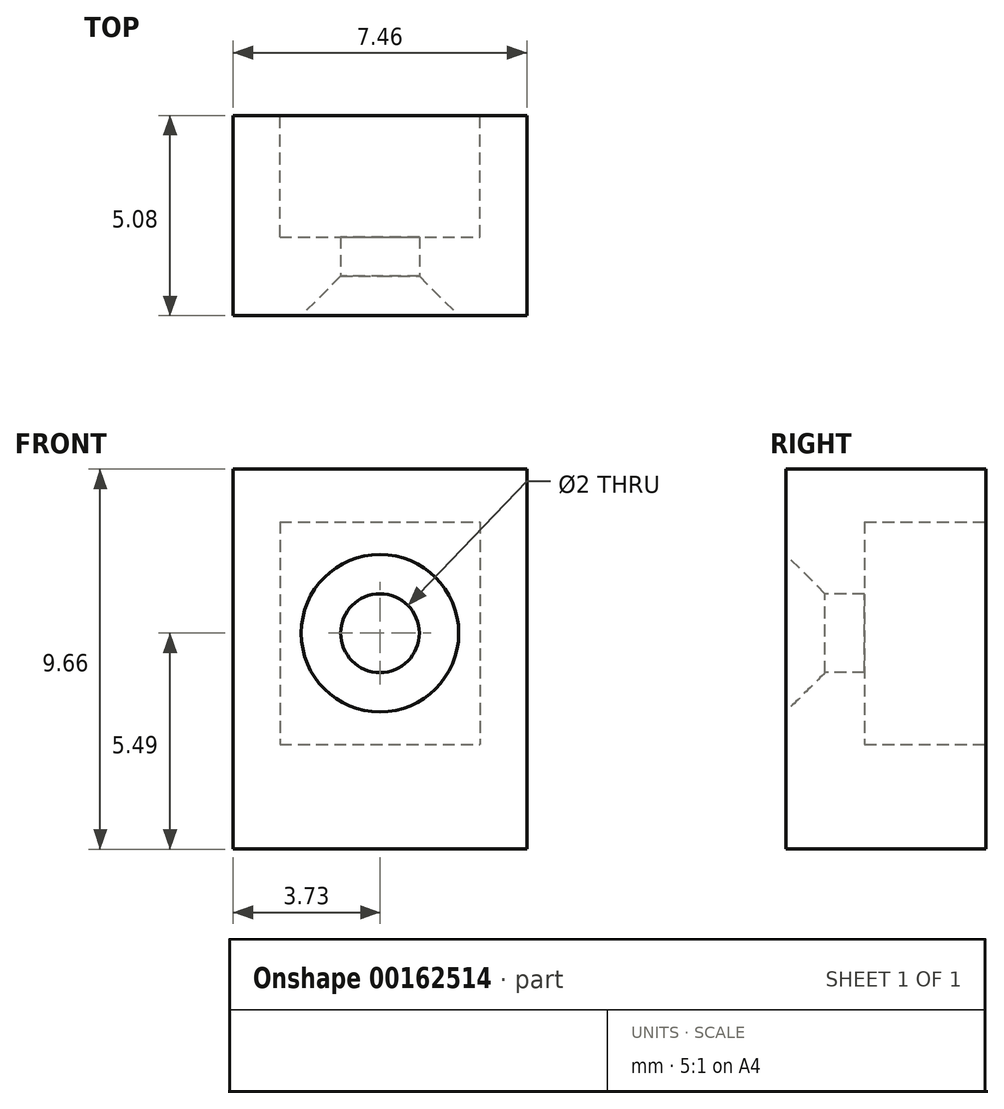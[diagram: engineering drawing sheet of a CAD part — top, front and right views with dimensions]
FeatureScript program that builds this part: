
annotation { "Feature Type Name" : "Feature", "Feature Type Description" : "" }
export const myFeature = defineFeature(function(context is Context, id is Id, definition is map)
    precondition{}
    {
        {
            var Q0;
            Q0=qCreatedBy(makeId("Front.planeOp"),FACE);
            var sketch = newSketch(context, id + "F0", { "sketchPlane" : qUnion([Q0])});
            skLineSegment(sketch, "E0.bottom", {"start": v(3.73, 4.83) * mm, "end": v(-3.73, 4.83) * mm});
            skLineSegment(sketch, "E0.top", {"start": v(3.73, -4.83) * mm, "end": v(-3.73, -4.83) * mm});
            skLineSegment(sketch, "E0.left", {"start": v(3.73, 4.83) * mm, "end": v(3.73, -4.83) * mm});
            skLineSegment(sketch, "E0.right", {"start": v(-3.73, 4.83) * mm, "end": v(-3.73, -4.83) * mm});
            skPoint(sketch, "E0.middle", {"position": v(0, 0) * mm});
            skCircle(sketch, "E1", {"center": v(0, 0.66) * mm, "radius": 1 * mm});
            skSolve(sketch);
        }
        {
            var Q0;
            Q0 = qSketchRegion(id + "F0", true);
            var Q1;
            Q1=makeQuery(id+"F0.imprint","IMPRINT",FACE,{"disambiguationData":[TD([[makeQuery(id+"F0.imprint","IMPRINT",EDGE,{"derivedFrom":sQuery(id+"F0.wireOp",EDGE,"E1")}),1.0]])]});
            extrude(context, id + "F1", {"entities" : qUnion([Q0, Q1]), "oppositeDirection" : true, "depth" : 5.08 * mm});
        }
        {
            var Q0;
            Q0=sQuery(id+"F0.wireOp",VERTEX,"E1.center");
            var Q1;
            Q1=makeQuery(id+"F1.opExtrude","SWEPT_BODY",BODY,{"disambiguationData":[OSD([sQuery(id+"F0.wireOp",EDGE,"E0.bottom"),sQuery(id+"F0.wireOp",EDGE,"E0.top"),sQuery(id+"F0.wireOp",EDGE,"E0.left"),sQuery(id+"F0.wireOp",EDGE,"E0.right")])]});
            hole(context, id + "F2", {"style" : HoleStyle.C_SINK, "endStyle" : HoleEndStyle.THROUGH, "holeDiameter" : 2 * mm, "cSinkDiameter" : 4 * mm, "cSinkAngle" : 90 * degree, "locations" : qUnion([Q0]), "scope" : qUnion([Q1]), "isTappedThrough" : true});
        }
        {
            var Q0;
            Q0=makeQuery(id+"F1.opExtrude","CAP_FACE",FACE,{"disambiguationData":[OSD([sQuery(id+"F0.wireOp",EDGE,"E0.bottom"),sQuery(id+"F0.wireOp",EDGE,"E0.top"),sQuery(id+"F0.wireOp",EDGE,"E0.left"),sQuery(id+"F0.wireOp",EDGE,"E0.right")])],"isStart":false});
            var sketch = newSketch(context, id + "F3", { "sketchPlane" : qUnion([Q0])});
            skCircle(sketch, "E2.0", {"center": v(0, 0.66) * mm, "radius": 1 * mm});
            skLineSegment(sketch, "E3.0", {"start": v(-3.73, 4.83) * mm, "end": v(3.73, 4.83) * mm});
            skLineSegment(sketch, "E4", {"start": v(2.82, 3.8) * mm, "end": v(-2.82, -2.48) * mm, "construction": true});
            skLineSegment(sketch, "E5", {"start": v(-2.82, 3.8) * mm, "end": v(2.82, -2.48) * mm, "construction": true});
            skLineSegment(sketch, "E6.bottom", {"start": v(2.54, 3.49) * mm, "end": v(-2.54, 3.49) * mm});
            skLineSegment(sketch, "E6.top", {"start": v(2.54, -2.17) * mm, "end": v(-2.54, -2.17) * mm});
            skLineSegment(sketch, "E6.left", {"start": v(2.54, 3.49) * mm, "end": v(2.54, -2.17) * mm});
            skLineSegment(sketch, "E6.right", {"start": v(-2.54, 3.49) * mm, "end": v(-2.54, -2.17) * mm});
            skSolve(sketch);
        }
        {
            var Q0;
            Q0 = qSketchRegion(id + "F3", true);
            extrude(context, id + "F4", {"entities" : qUnion([Q0]), "operationType" : NewBodyOperationType.REMOVE, "oppositeDirection" : true, "depth" : 3.08 * mm});
        }
    });
